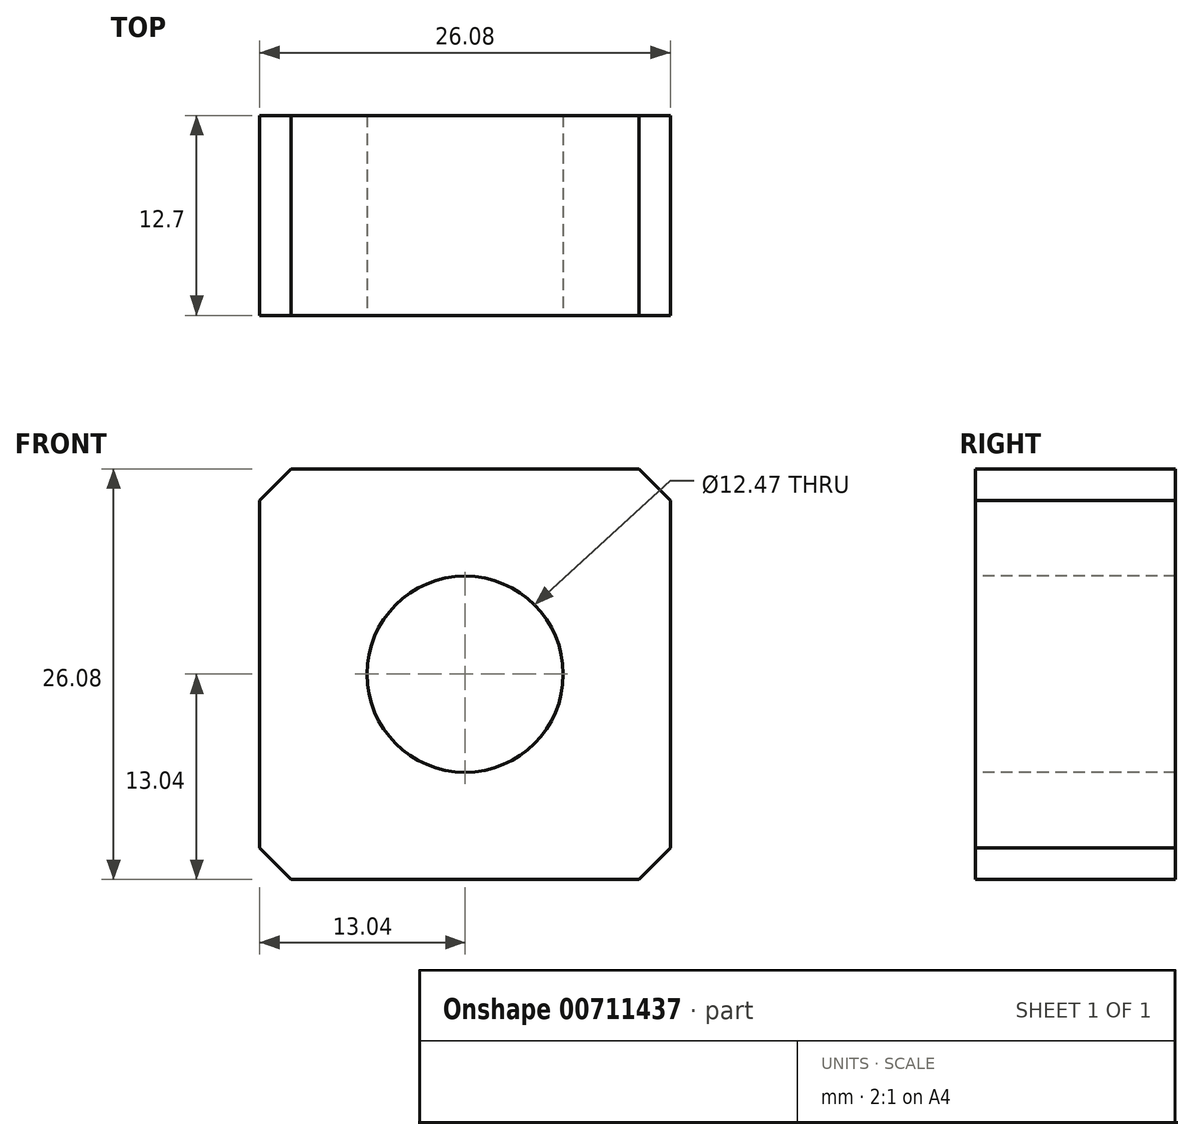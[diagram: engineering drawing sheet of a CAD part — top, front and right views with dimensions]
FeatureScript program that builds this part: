
annotation { "Feature Type Name" : "Feature", "Feature Type Description" : "" }
export const myFeature = defineFeature(function(context is Context, id is Id, definition is map)
    precondition{}
    {
        {
            var Q0;
            Q0=qCreatedBy(makeId("Front.planeOp"),FACE);
            var sketch = newSketch(context, id + "F0", { "sketchPlane" : qUnion([Q0])});
            skLineSegment(sketch, "E0.bottom", {"start": v(13.04, 13.04) * mm, "end": v(-13.04, 13.04) * mm});
            skLineSegment(sketch, "E0.top", {"start": v(13.04, -13.04) * mm, "end": v(-13.04, -13.04) * mm});
            skLineSegment(sketch, "E0.left", {"start": v(13.04, 13.04) * mm, "end": v(13.04, -13.04) * mm});
            skLineSegment(sketch, "E0.right", {"start": v(-13.04, 13.04) * mm, "end": v(-13.04, -13.04) * mm});
            skPoint(sketch, "E0.middle", {"position": v(0, 0) * mm});
            skSolve(sketch);
        }
        {
            var Q0;
            Q0 = qSketchRegion(id + "F0", true);
            extrude(context, id + "F1", {"entities" : qUnion([Q0]), "depth" : (25.4 / 2) * mm, "offsetDistance" : 25 * mm});
        }
        {
            var Q0;
            Q0=makeQuery(id+"F1.opExtrude","CAP_FACE",FACE,{"disambiguationData":[OSD([sQuery(id+"F0.wireOp",EDGE,"E0.bottom"),sQuery(id+"F0.wireOp",EDGE,"E0.top"),sQuery(id+"F0.wireOp",EDGE,"E0.left"),sQuery(id+"F0.wireOp",EDGE,"E0.right")])],"isStart":false});
            var sketch = newSketch(context, id + "F2", { "sketchPlane" : qUnion([Q0])});
            skCircle(sketch, "E1", {"center": v(0, 0) * mm, "radius": 6.23 * mm});
            skSolve(sketch);
        }
        {
            var Q0;
            Q0 = qSketchRegion(id + "F2", true);
            extrude(context, id + "F3", {"entities" : qUnion([Q0]), "operationType" : NewBodyOperationType.REMOVE, "endBound" : BoundingType.THROUGH_ALL, "oppositeDirection" : true, "depth" : 25 * mm, "offsetDistance" : 25 * mm});
        }
        {
            var Q0;
            Q0=makeQuery(id+"F1.opExtrude","SWEPT_EDGE",EDGE,{"disambiguationData":[OSD([sQuery(id+"F0.wireOp",EDGE,"E0.top"),sQuery(id+"F0.wireOp",EDGE,"E0.left")])]});
            var Q1;
            Q1=makeQuery(id+"F1.opExtrude","SWEPT_EDGE",EDGE,{"disambiguationData":[OSD([sQuery(id+"F0.wireOp",EDGE,"E0.bottom"),sQuery(id+"F0.wireOp",EDGE,"E0.left")])]});
            var Q2;
            Q2=makeQuery(id+"F1.opExtrude","SWEPT_EDGE",EDGE,{"disambiguationData":[OSD([sQuery(id+"F0.wireOp",EDGE,"E0.top"),sQuery(id+"F0.wireOp",EDGE,"E0.right")])]});
            var Q3;
            Q3=makeQuery(id+"F1.opExtrude","SWEPT_EDGE",EDGE,{"disambiguationData":[OSD([sQuery(id+"F0.wireOp",EDGE,"E0.bottom"),sQuery(id+"F0.wireOp",EDGE,"E0.right")])]});
            chamfer(context, id + "F4", {"entities" : qUnion([Q0, Q1, Q2, Q3]), "width" : 2 * mm, "tangentPropagation" : true});
        }
    });
